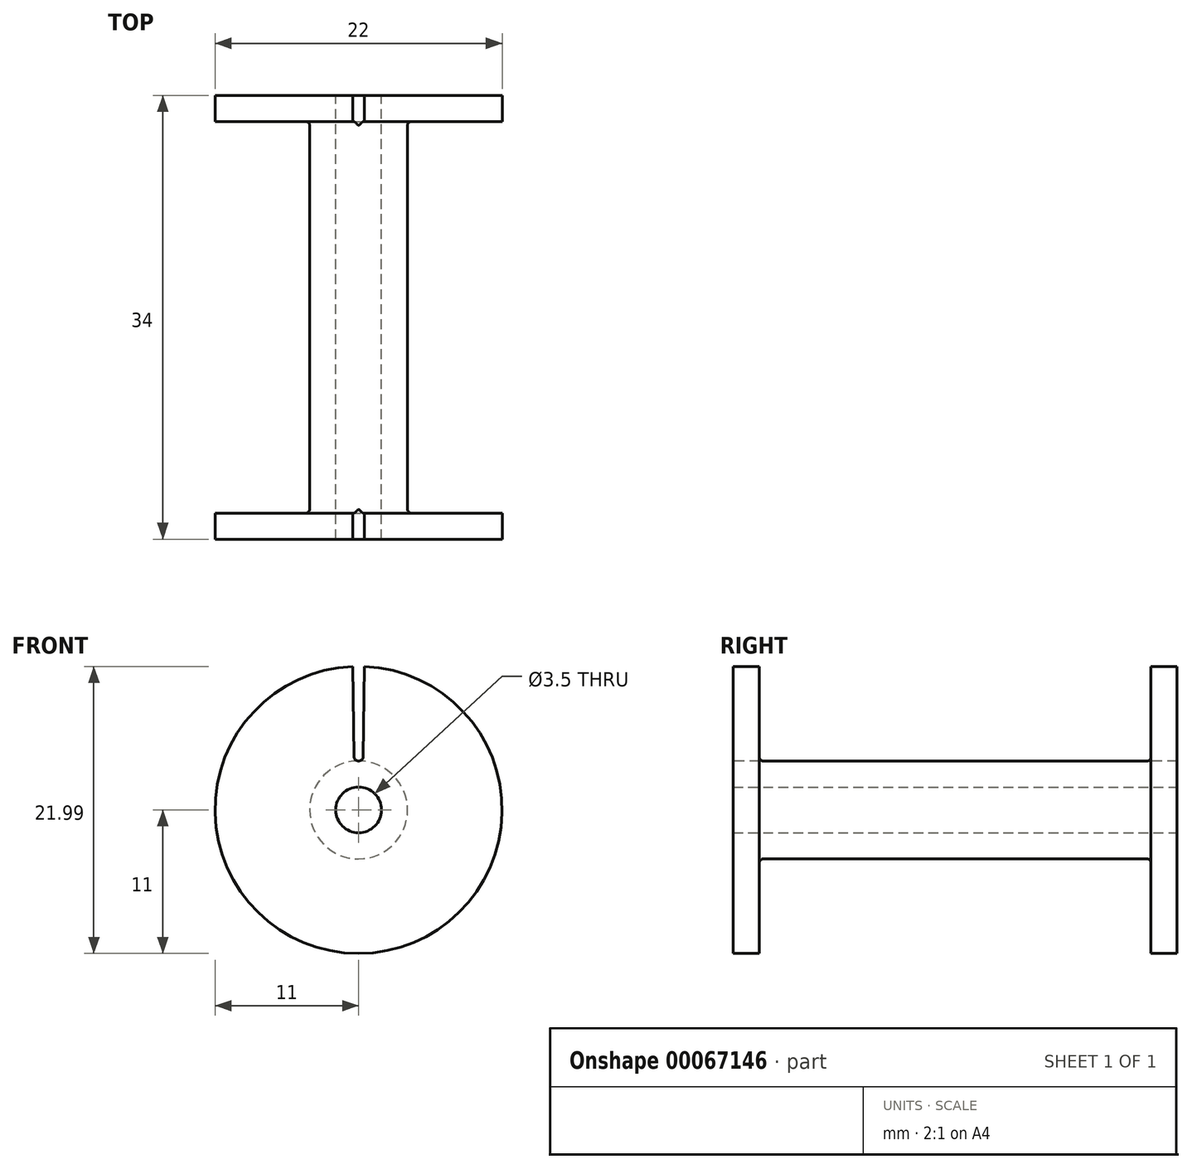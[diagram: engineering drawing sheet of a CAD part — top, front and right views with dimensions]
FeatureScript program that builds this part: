
annotation { "Feature Type Name" : "Feature", "Feature Type Description" : "" }
export const myFeature = defineFeature(function(context is Context, id is Id, definition is map)
    precondition{}
    {
        {
            var Q0;
            Q0=qCreatedBy(makeId("Top.planeOp"),FACE);
            var sketch = newSketch(context, id + "F0", { "sketchPlane" : qUnion([Q0])});
            skLineSegment(sketch, "E0", {"start": v(0, 12.85) * mm, "end": v(0, -12.45) * mm, "construction": true});
            skLineSegment(sketch, "E1", {"start": v(-12.93, 0) * mm, "end": v(12.88, 0) * mm, "construction": true});
            skLineSegment(sketch, "E2.bottom", {"start": v(-11, 17) * mm, "end": v(-1.75, 17) * mm});
            skLineSegment(sketch, "E2.top", {"start": v(-11, -17) * mm, "end": v(-1.75, -17) * mm});
            skLineSegment(sketch, "E2.left", {"start": v(-11, 17) * mm, "end": v(-11, 15) * mm});
            skLineSegment(sketch, "E2.right", {"start": v(-1.75, 17) * mm, "end": v(-1.75, -17) * mm});
            skLineSegment(sketch, "E3.bottom", {"start": v(-11, 15) * mm, "end": v(-3.75, 15) * mm});
            skLineSegment(sketch, "E3.top", {"start": v(-11, -15) * mm, "end": v(-3.75, -15) * mm});
            skLineSegment(sketch, "E3.right", {"start": v(-3.75, 15) * mm, "end": v(-3.75, -15) * mm});
            skLineSegment(sketch, "E4.trimOffspring", {"start": v(-11, -15) * mm, "end": v(-11, -17) * mm});
            skSolve(sketch);
        }
        {
            var Q0;
            Q0=makeQuery(id+"F0.imprint","IMPRINT",FACE,{"disambiguationData":[TD([[makeQuery(id+"F0.imprint","IMPRINT",EDGE,{"derivedFrom":sQuery(id+"F0.wireOp",EDGE,"E2.bottom")}),-1.0]])]});
            var Q1;
            Q1=sQuery(id+"F0.wireOp",EDGE,"E0");
            revolve(context, id + "F1", {"entities" : qUnion([Q0]), "axis" : qUnion([Q1]), "revolveType" : RevolveType.FULL});
        }
        {
            var Q0;
            Q0=makeQuery(id+"F1.opRevolve","SWEPT_FACE",FACE,{"disambiguationData":[OSD([sQuery(id+"F0.wireOp",EDGE,"E2.top")])]});
            var sketch = newSketch(context, id + "F2", { "sketchPlane" : qUnion([Q0])});
            skLineSegment(sketch, "E5", {"start": v(0, 11) * mm, "end": v(0, -11) * mm, "construction": true});
            skLineSegment(sketch, "E6", {"start": v(11, 0) * mm, "end": v(-11, 0) * mm, "construction": true});
            skLineSegment(sketch, "E7", {"start": v(0.45, 11) * mm, "end": v(-0.45, 11) * mm});
            skLineSegment(sketch, "E8", {"start": v(0, 3.75) * mm, "end": v(0, 3.75) * mm});
            skLineSegment(sketch, "E9", {"start": v(-0.45, 11) * mm, "end": v(-0.35, 4.1) * mm});
            skLineSegment(sketch, "E10", {"start": v(0.45, 11) * mm, "end": v(0.35, 4.1) * mm});
            skPoint(sketch, "E11.visualSharp", {"position": v(-0.35, 3.75) * mm});
            skArc(sketch, "E11.filletArc", {"start": v(-0.35, 4.1) * mm, "mid": v(-0.25, 3.85) * mm, "end": v(0, 3.75) * mm});
            skPoint(sketch, "E12.visualSharp", {"position": v(0.35, 3.75) * mm});
            skArc(sketch, "E12.filletArc", {"start": v(0, 3.75) * mm, "mid": v(0.25, 3.85) * mm, "end": v(0.35, 4.1) * mm});
            skSolve(sketch);
        }
        {
            var Q0;
            Q0=makeQuery(id+"F2.imprint","IMPRINT",FACE,{"disambiguationData":[TD([[makeQuery(id+"F2.imprint","IMPRINT",EDGE,{"derivedFrom":sQuery(id+"F2.wireOp",EDGE,"E8")}),-1.0]])]});
            extrude(context, id + "F3", {"entities" : qUnion([Q0]), "operationType" : NewBodyOperationType.REMOVE, "endBound" : BoundingType.THROUGH_ALL, "oppositeDirection" : true, "depth" : 25 * mm});
        }
        {
            var Q0;
            Q0=makeQuery(id+"F3.boolean.opBoolean","SPLIT",EDGE,{"disambiguationData":[OD(0.0)],"derivedFrom":makeQuery(id+"F1.opRevolve","SWEPT_EDGE",EDGE,{"disambiguationData":[OSD([sQuery(id+"F0.wireOp",EDGE,"E3.top"),sQuery(id+"F0.wireOp",EDGE,"E3.right")])]})});
            var Q1;
            Q1=makeQuery(id+"F3.boolean.opBoolean","SPLIT",EDGE,{"disambiguationData":[OD(0.0)],"derivedFrom":makeQuery(id+"F1.opRevolve","SWEPT_EDGE",EDGE,{"disambiguationData":[OSD([sQuery(id+"F0.wireOp",EDGE,"E3.bottom"),sQuery(id+"F0.wireOp",EDGE,"E3.right")])]})});
            fillet(context, id + "F4", {"entities" : qUnion([Q0, Q1]), "radius" : .3 * mm, "tangentPropagation" : true, "allowEdgeOverflow" : false});
        }
    });
